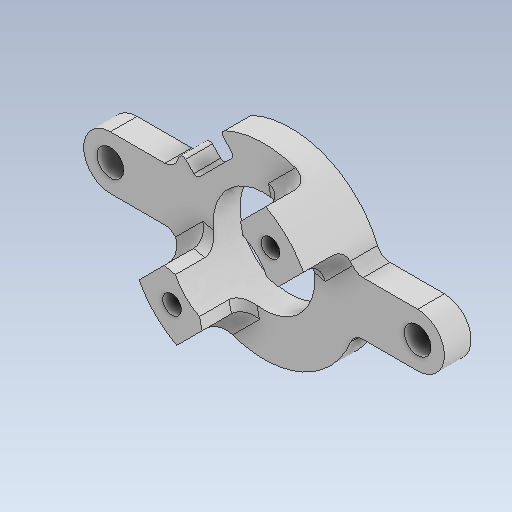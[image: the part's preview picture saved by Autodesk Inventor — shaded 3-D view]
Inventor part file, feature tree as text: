
AUTODESK INVENTOR PART (.ipt)
format: ipt  version: 2020 (Build 240168000, 168)  size: 322,048 bytes
history: native  units: mm
features: extrude x4, thicken_offset x4, sketch x4, fillet x3, projected_geometry x3, other x3, reference x2, chamfer x1
ambient origin geometry x8: Origin, YZ Plane, XZ Plane, XY Plane, X Axis, Y Axis, Z Axis, Center Point
bodies: Solid1 (feature_tree)
feature tree (24):
  extrude  "Extrusion1"  Depth=4.0mm
  extrude  "Extrusion2"  Depth=2.0mm TaperAngle=0.0deg
  thicken_offset  "Thicken1"
  chamfer  "Chamfer1"  Distance=5.207mm
  fillet  "Fillet1"  Radius=1.4mm
  fillet  "Fillet2"  Radius=1.4mm
  extrude  "Extrusion3"  Depth=2.0mm
  extrude  "Extrusion4"  Depth=2.0mm
  fillet  "Fillet3"  Radius=2.0mm
  thicken_offset  "Thicken2"
  thicken_offset  "Thicken3"
  thicken_offset  "Thicken4"
  sketch  "Sketch1"  dims[d0=4.0mm d1=7.8mm]
  reference  "Reference1"
  sketch  "Sketch2"  dims[d2=14.0mm d3=2.0mm d4=0.0mm]
  projected_geometry  "Projected Loop1"
  sketch  "Sketch3"  dims[d5=5.207mm]
  projected_geometry  "Projected Loop2"
  projected_geometry  "Projected Loop3"
  sketch  "Sketch4"  dims[d6=45.0deg d7=5.207mm d8=1.4mm d9=1.4mm d10=2.0mm d11=2.0mm d12=2.0mm d13=2.0mm d14=2.7mm d15=0.0mm d16=0.1mm d17=0.1mm d18=0.8mm d19=2.0mm d20=45.0deg d21=1.0mm d22=1.0mm d23=2.7mm d24=0.0mm d25=2.7mm d26=0.0mm d27=0.3mm d28=0.5mm d29=0.5mm d30=0.5mm d31=0.5mm d32=0.5mm d33=0.5mm]
  reference  "Reference2"
  parser-record x1  (decoder bookkeeping rows leaked as tree rows — omitted from the tree; the rows remain in map.json)
  other  "reducer_1.iam"
  other  "mot_holder_1:1"
note: 1 file-system path scrubbed to <path> (originals preserved in map.json)
